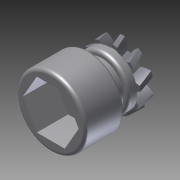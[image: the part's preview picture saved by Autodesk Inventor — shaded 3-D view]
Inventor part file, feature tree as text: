
AUTODESK INVENTOR PART (.ipt)
format: ipt  version: 2012 (Build 160160000, 160)  size: 604,672 bytes
history: native  units: in
note: dims shown in document units (in); Inventor stores cm internally (conversion verified against a paired STEP export)
features: fillet x8, extrude x6, sketch x6, other x3, plane x1
ambient origin geometry x8: Origin, YZ Plane, XZ Plane, XY Plane, X Axis, Y Axis, Z Axis, Center Point
bodies: Solid2 (feature_tree)
feature tree (24):
  other  "SmallOutputGear.iam"
  other  "BlankSmallGearOutput.ipt:1"
  other  "Spur Gear1:1"
  extrude  "Extrusion3"  Depth=0.0276in TaperAngle=0.0deg
  extrude  "Extrusion4"  Depth=0.3937in TaperAngle=0.0deg
  extrude  "Extrusion5"  Depth=0.3937in TaperAngle=0.0deg
  extrude  "Extrusion6"  Depth=0.3937in TaperAngle=0.0deg
  extrude  "Extrusion7"  Depth=0.3937in TaperAngle=0.0deg
  extrude  "Extrusion9"  Depth=0.0591in TaperAngle=0.0deg
  fillet  "Fillet8"  Radius=0.0197in
  fillet  "Fillet9"  Radius=0.0394in
  fillet  "Fillet10"  Radius=0.0394in
  fillet  "Fillet11"  Radius=0.0079in
  fillet  "Fillet12"  Radius=0.0197in
  fillet  "Fillet13"  Radius=0.1181in
  fillet  "Fillet14"  Radius=0.0394in
  fillet  "Fillet15"  Radius=0.0394in
  plane  "Work Plane4"
  sketch  "Sketch5"  dims[d5=0.3937in d6=0.0276in d7=0.0in]
  sketch  "Sketch6"  dims[d8=0.0591in d9=0.3937in d10=0.0in]
  sketch  "Sketch7"  dims[d11=0.0591in d12=0.3937in d13=0.0in]
  sketch  "Sketch8"  dims[d14=0.6299in d15=0.3937in d16=0.0in]
  sketch  "Sketch9"  dims[d17=0.0591in d18=0.3937in d19=0.0in]
  sketch  "Sketch11"  dims[d34=0.0591in d35=0.0591in d36=0.1575in d37=0.0in d38=0.0in d39=0.0197in d40=0.0394in d41=0.0394in d42=0.0079in d43=0.0197in d44=0.1181in d45=0.0394in d46=0.0394in]
